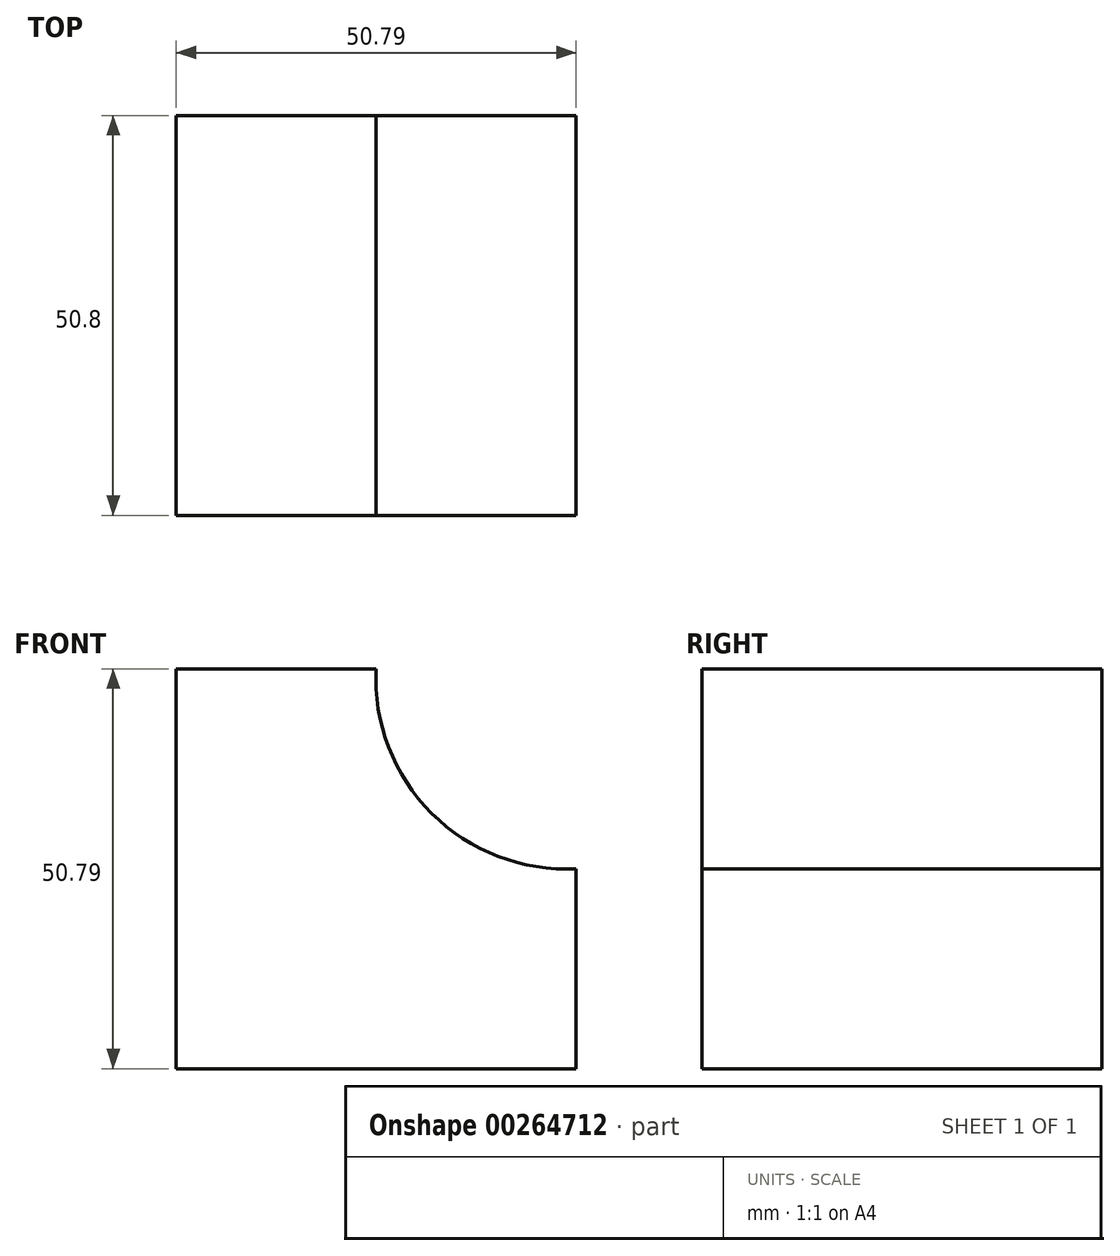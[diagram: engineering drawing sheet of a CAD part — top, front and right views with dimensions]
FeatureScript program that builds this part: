
annotation { "Feature Type Name" : "Feature", "Feature Type Description" : "" }
export const myFeature = defineFeature(function(context is Context, id is Id, definition is map)
    precondition{}
    {
        {
            var Q0;
            Q0=qCreatedBy(makeId("Front.planeOp"),FACE);
            var sketch = newSketch(context, id + "F0", { "sketchPlane" : qUnion([Q0])});
            skLineSegment(sketch, "E0", {"start": v(0, 0) * mm, "end": v(-50.8, 0) * mm});
            skLineSegment(sketch, "E1", {"start": v(-50.8, 0) * mm, "end": v(-50.8, 25.4) * mm});
            skLineSegment(sketch, "E2", {"start": v(-50.8, 25.4) * mm, "end": v(-50.8, 50.8) * mm});
            skLineSegment(sketch, "E3", {"start": v(-50.8, 50.8) * mm, "end": v(-25.4, 50.8) * mm});
            skLineSegment(sketch, "E4", {"start": v(0, 0) * mm, "end": v(0, 25.4) * mm});
            skArc(sketch, "E5", {"start": v(-25.4, 50.8) * mm, "mid": v(-18.35, 32.45) * mm, "end": v(0, 25.4) * mm});
            skSolve(sketch);
        }
        {
            var Q0;
            Q0 = qSketchRegion(id + "F0", true);
            extrude(context, id + "F1", {"entities" : qUnion([Q0]), "depth" : 50.8 * mm});
        }
    });
